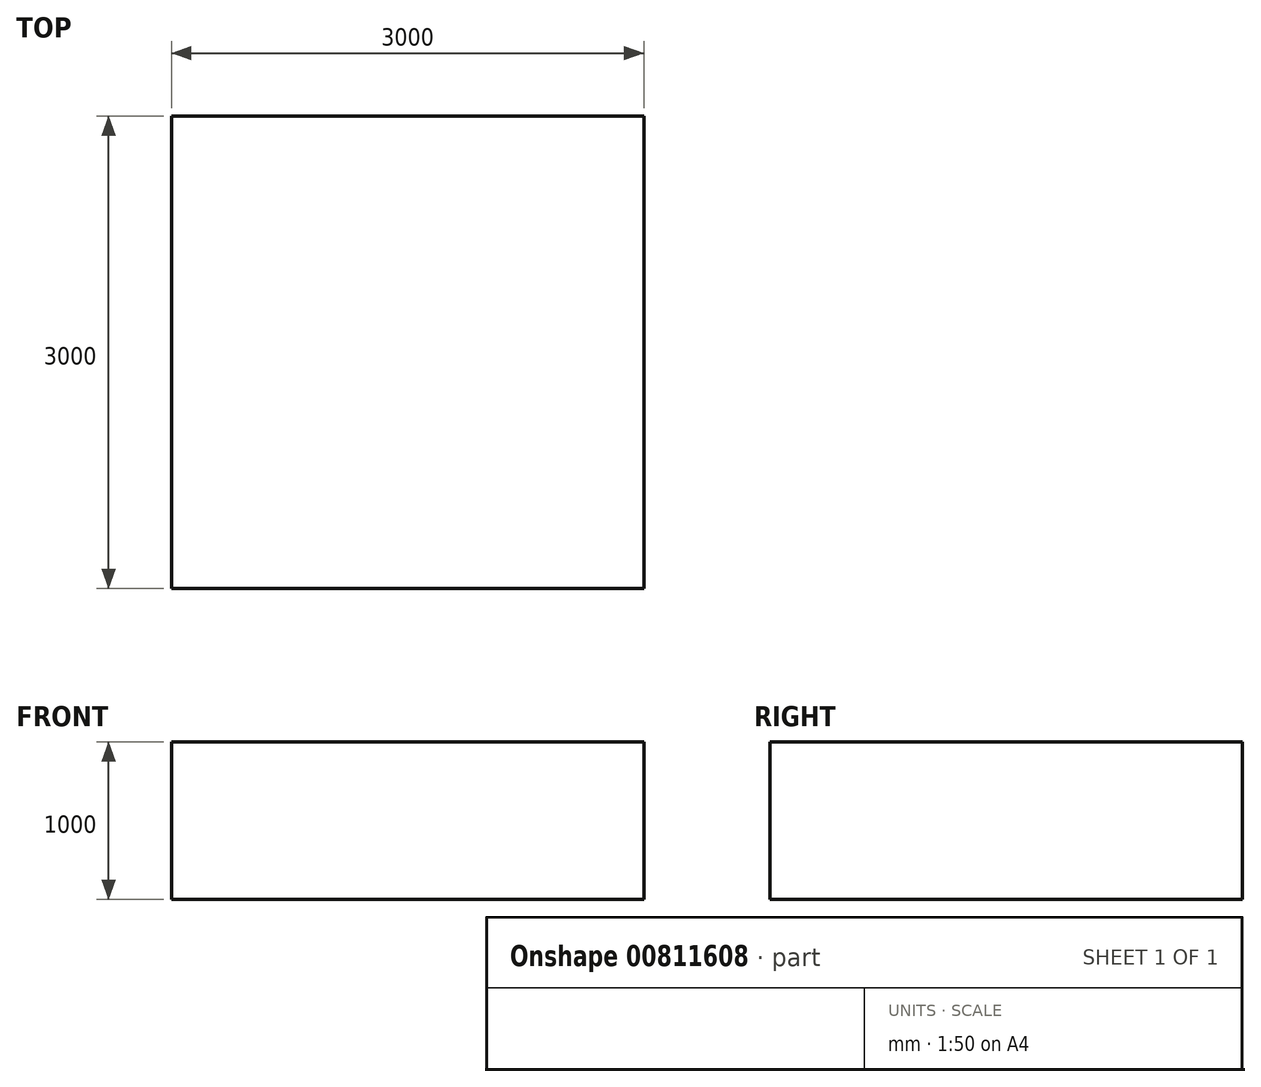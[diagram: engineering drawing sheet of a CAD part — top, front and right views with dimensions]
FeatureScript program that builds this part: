
annotation { "Feature Type Name" : "Feature", "Feature Type Description" : "" }
export const myFeature = defineFeature(function(context is Context, id is Id, definition is map)
    precondition{}
    {
        {
            var Q0;
            Q0=qCreatedBy(makeId("Top.planeOp"),FACE);
            var sketch = newSketch(context, id + "F0", { "sketchPlane" : qUnion([Q0])});
            skLineSegment(sketch, "E0.bottom", {"start": v(-101.47, 2765.72) * mm, "end": v(2898.53, 2765.72) * mm});
            skLineSegment(sketch, "E0.top", {"start": v(-101.47, -234.28) * mm, "end": v(2898.53, -234.28) * mm});
            skLineSegment(sketch, "E0.left", {"start": v(-101.47, 2765.72) * mm, "end": v(-101.47, -234.28) * mm});
            skLineSegment(sketch, "E0.right", {"start": v(2898.53, 2765.72) * mm, "end": v(2898.53, -234.28) * mm});
            skSolve(sketch);
        }
        {
            var Q0;
            Q0 = qSketchRegion(id + "F0", true);
            extrude(context, id + "F1", {"entities" : qUnion([Q0]), "depth" : 1000 * mm, "offsetDistance" : 25 * mm});
        }
    });
